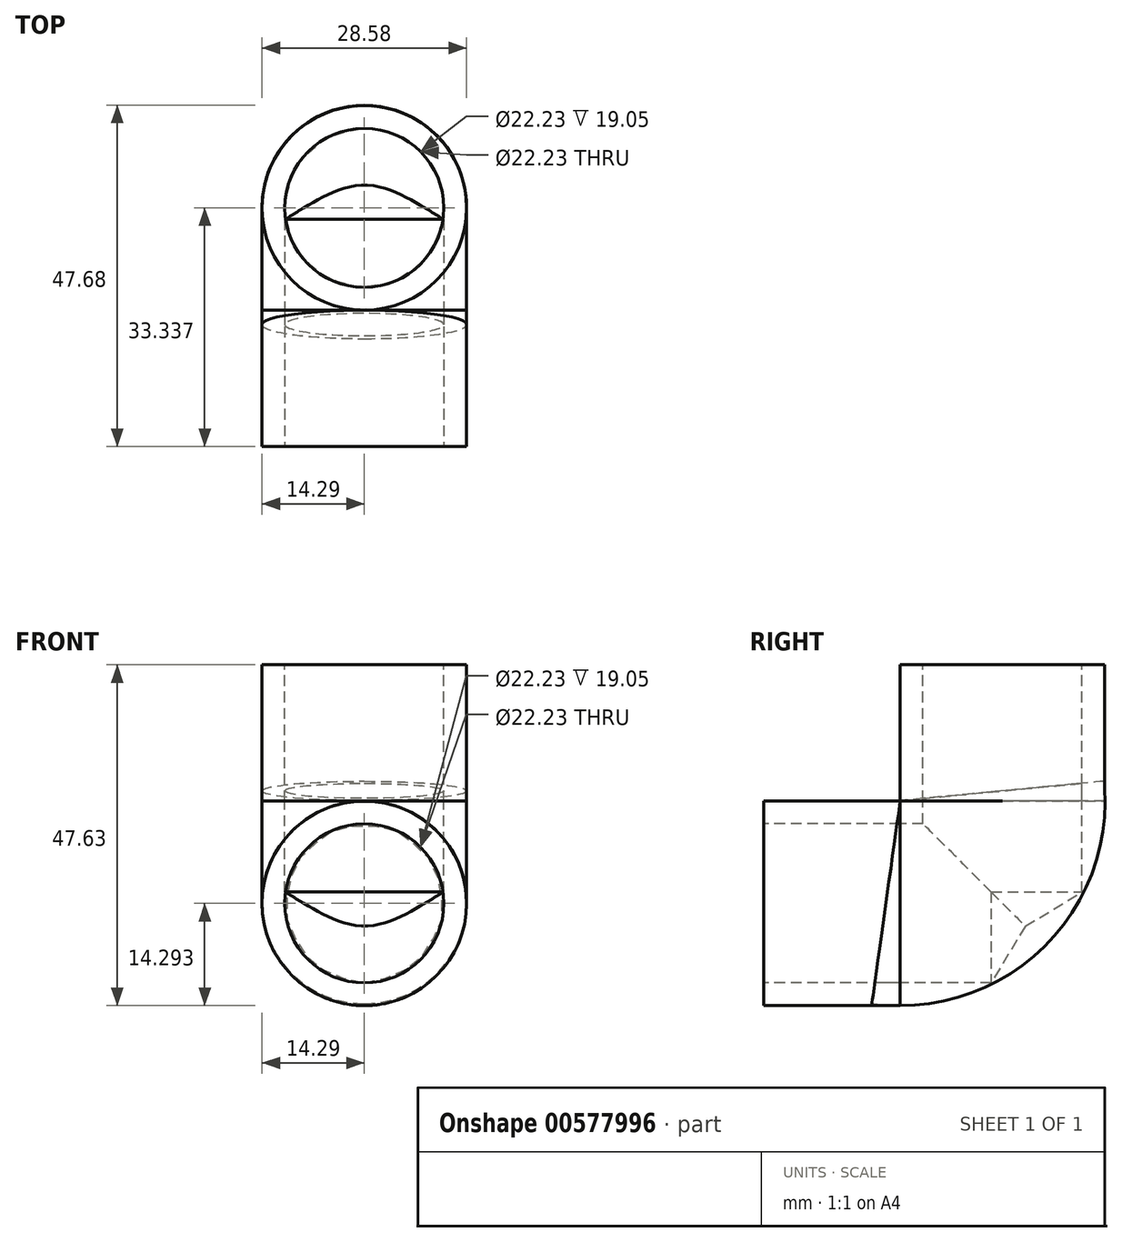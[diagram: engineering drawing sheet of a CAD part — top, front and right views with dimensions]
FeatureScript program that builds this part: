
annotation { "Feature Type Name" : "Feature", "Feature Type Description" : "" }
export const myFeature = defineFeature(function(context is Context, id is Id, definition is map)
    precondition{}
    {
        {
            var Q0;
            Q0=qCreatedBy(makeId("Top.planeOp"),FACE);
            var sketch = newSketch(context, id + "F0", { "sketchPlane" : qUnion([Q0])});
            skCircle(sketch, "E0", {"center": v(0, 33.34) * mm, "radius": 14.29 * mm});
            skSolve(sketch);
        }
        {
            var Q0;
            Q0=qCreatedBy(makeId("Front.planeOp"),FACE);
            var sketch = newSketch(context, id + "F1", { "sketchPlane" : qUnion([Q0])});
            skCircle(sketch, "E1", {"center": v(0, -33.34) * mm, "radius": 14.29 * mm});
            skSolve(sketch);
        }
        {
            var Q0;
            Q0=makeQuery(id+"F1.imprint","IMPRINT",FACE,{"disambiguationData":[TD([[makeQuery(id+"F1.imprint","IMPRINT",EDGE,{"derivedFrom":sQuery(id+"F1.wireOp",EDGE,"E1")}),1.0]])]});
            extrude(context, id + "F2", {"entities" : qUnion([Q0]), "flatOperationType" : FlatOperationType.REMOVE, "oppositeDirection" : true, "offsetDistance" : 25.4 * mm, "depth" : 19.05 * mm, "domain" : OperationDomain.MODEL});
        }
        {
            var Q0;
            Q0=makeQuery(id+"F0.imprint","IMPRINT",FACE,{"disambiguationData":[TD([[makeQuery(id+"F0.imprint","IMPRINT",EDGE,{"derivedFrom":sQuery(id+"F0.wireOp",EDGE,"E0")}),1.0]])]});
            extrude(context, id + "F3", {"entities" : qUnion([Q0]), "operationType" : NewBodyOperationType.ADD, "oppositeDirection" : true, "depth" : 19.05 * mm});
        }
        {
            var Q0;
            Q0=qCreatedBy(makeId("Right.planeOp"),FACE);
            var sketch = newSketch(context, id + "F4", { "sketchPlane" : qUnion([Q0])});
            skArc(sketch, "E2", {"start": v(17.12, -32.73) * mm, "mid": v(28.64, -29.01) * mm, "end": v(32.85, -17.67) * mm});
            skSolve(sketch);
        }
        {
            var Q0;
            Q0=makeQuery(id+"F2.opExtrude","CAP_FACE",FACE,{"disambiguationData":[OSD([sQuery(id+"F1.wireOp",EDGE,"E1")])],"isStart":false});
            var Q1;
            Q1=sQuery(id+"F4.wireOp",EDGE,"E2");
            sweep(context, id + "F5", {"profiles" : qUnion([Q0]), "path" : qUnion([Q1])});
        }
        {
            var Q0;
            Q0=makeQuery(id+"F3.opExtrude","CAP_FACE",FACE,{"disambiguationData":[OSD([sQuery(id+"F0.wireOp",EDGE,"E0")])],"isStart":true});
            var sketch = newSketch(context, id + "F6", { "sketchPlane" : qUnion([Q0])});
            skCircle(sketch, "E3", {"center": v(0, 33.34) * mm, "radius": 11.11 * mm});
            skSolve(sketch);
        }
        {
            var Q0;
            Q0=sQuery(id+"F6.wireOp",VERTEX,"E3.center");
            var Q1;
            Q1=makeQuery(id+"F3.opExtrude","SWEPT_BODY",BODY,{"disambiguationData":[OSD([sQuery(id+"F0.wireOp",EDGE,"E0")])]});
            var Q2;
            Q2=makeQuery(id+"F5.opSweep","SWEPT_BODY",BODY,{"disambiguationData":[OSD([sQuery(id+"F1.wireOp",EDGE,"E1"),sQuery(id+"F4.wireOp",EDGE,"E2")])]});
            hole(context, id + "F7", {"style" : HoleStyle.SIMPLE, "endStyle" : HoleEndStyle.BLIND, "holeDiameter" : 22.22 * mm, "holeDepth" : 31.75 * mm, "tappedDepth" : 12.7 * mm, "tapClearance" : 3, "locations" : qUnion([Q0]), "scope" : qUnion([Q1, Q2])});
        }
        {
            var Q0;
            Q0=makeQuery(id+"F2.opExtrude","CAP_FACE",FACE,{"disambiguationData":[OSD([sQuery(id+"F1.wireOp",EDGE,"E1")])],"isStart":true});
            var sketch = newSketch(context, id + "F8", { "sketchPlane" : qUnion([Q0])});
            skCircle(sketch, "E4", {"center": v(0, -33.34) * mm, "radius": 11.11 * mm});
            skSolve(sketch);
        }
        {
            var Q0;
            Q0=sQuery(id+"F8.wireOp",VERTEX,"E4.center");
            var Q1;
            Q1=makeQuery(id+"F2.opExtrude","SWEPT_BODY",BODY,{"disambiguationData":[OSD([sQuery(id+"F1.wireOp",EDGE,"E1")])]});
            var Q2;
            Q2=makeQuery(id+"F5.opSweep","SWEPT_BODY",BODY,{"disambiguationData":[OSD([sQuery(id+"F1.wireOp",EDGE,"E1"),sQuery(id+"F4.wireOp",EDGE,"E2")])]});
            hole(context, id + "F9", {"style" : HoleStyle.SIMPLE, "endStyle" : HoleEndStyle.BLIND, "holeDiameter" : 22.22 * mm, "holeDepth" : 31.75 * mm, "tappedDepth" : 12.7 * mm, "tapClearance" : 3, "locations" : qUnion([Q0]), "scope" : qUnion([Q1, Q2])});
        }
    });
